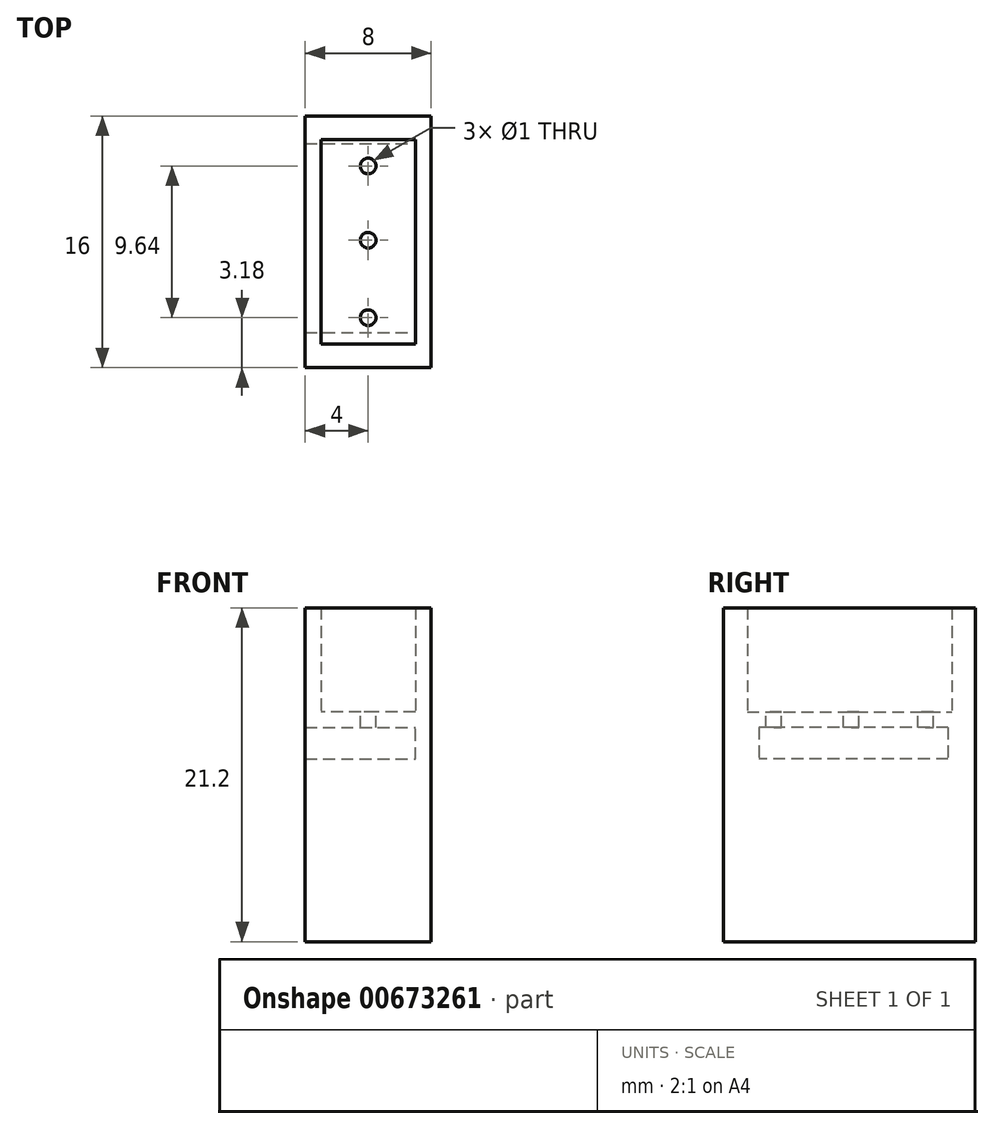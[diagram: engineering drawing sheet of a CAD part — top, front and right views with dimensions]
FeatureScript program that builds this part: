
annotation { "Feature Type Name" : "Feature", "Feature Type Description" : "" }
export const myFeature = defineFeature(function(context is Context, id is Id, definition is map)
    precondition{}
    {
        {
            var Q0;
            Q0=qCreatedBy(makeId("Top.planeOp"),FACE);
            var sketch = newSketch(context, id + "F0", { "sketchPlane" : qUnion([Q0])});
            skLineSegment(sketch, "E0.bottom", {"start": v(0, 0) * mm, "end": v(-6, 0) * mm});
            skLineSegment(sketch, "E0.top", {"start": v(0, 13) * mm, "end": v(-6, 13) * mm});
            skLineSegment(sketch, "E0.left", {"start": v(0, 0) * mm, "end": v(0, 13) * mm});
            skLineSegment(sketch, "E0.right", {"start": v(-6, 0) * mm, "end": v(-6, 13) * mm});
            skLineSegment(sketch, "E1.bottom", {"start": v(1, -1.5) * mm, "end": v(-7, -1.5) * mm});
            skLineSegment(sketch, "E1.top", {"start": v(1, 14.5) * mm, "end": v(-7, 14.5) * mm});
            skLineSegment(sketch, "E1.left", {"start": v(1, -1.5) * mm, "end": v(1, 14.5) * mm});
            skLineSegment(sketch, "E1.right", {"start": v(-7, -1.5) * mm, "end": v(-7, 14.5) * mm});
            skSolve(sketch);
        }
        {
            var Q0;
            Q0 = qSketchRegion(id + "F0", true);
            extrude(context, id + "F1", {"entities" : qUnion([Q0]), "depth" : 6.6 * mm, "offsetDistance" : 25 * mm});
        }
        {
            var Q0;
            Q0=makeQuery(id+"F1.opExtrude","CAP_FACE",FACE,{"disambiguationData":[OSD([sQuery(id+"F0.wireOp",EDGE,"E0.bottom"),sQuery(id+"F0.wireOp",EDGE,"E0.top"),sQuery(id+"F0.wireOp",EDGE,"E0.left"),sQuery(id+"F0.wireOp",EDGE,"E0.right"),sQuery(id+"F0.wireOp",EDGE,"E1.bottom"),sQuery(id+"F0.wireOp",EDGE,"E1.top"),sQuery(id+"F0.wireOp",EDGE,"E1.left"),sQuery(id+"F0.wireOp",EDGE,"E1.right")])],"isStart":true});
            var sketch = newSketch(context, id + "F2", { "sketchPlane" : qUnion([Q0])});
            skLineSegment(sketch, "E2.bottom", {"start": v(-7, 1.5) * mm, "end": v(1, 1.5) * mm});
            skLineSegment(sketch, "E2.top", {"start": v(-7, -14.5) * mm, "end": v(1, -14.5) * mm});
            skLineSegment(sketch, "E2.left", {"start": v(-7, 1.5) * mm, "end": v(-7, -14.5) * mm});
            skLineSegment(sketch, "E2.right", {"start": v(1, 1.5) * mm, "end": v(1, -14.5) * mm});
            skSolve(sketch);
        }
        {
            var Q0;
            Q0 = qSketchRegion(id + "F2", true);
            extrude(context, id + "F3", {"entities" : qUnion([Q0]), "operationType" : NewBodyOperationType.ADD, "depth" : 14.6 * mm, "offsetDistance" : 25 * mm});
        }
        {
            var Q0;
            Q0=qCreatedBy(makeId("Right.planeOp"),FACE);
            var sketch = newSketch(context, id + "F4", { "sketchPlane" : qUnion([Q0])});
            skLineSegment(sketch, "E3.bottom", {"start": v(0.75, -3) * mm, "end": v(12.75, -3) * mm});
            skLineSegment(sketch, "E3.top", {"start": v(0.75, -1) * mm, "end": v(12.75, -1) * mm});
            skLineSegment(sketch, "E3.left", {"start": v(0.75, -3) * mm, "end": v(0.75, -1) * mm});
            skLineSegment(sketch, "E3.right", {"start": v(12.75, -3) * mm, "end": v(12.75, -1) * mm});
            skSolve(sketch);
        }
        {
            var Q0;
            Q0=makeQuery(id+"F3.opExtrude","CAP_FACE",FACE,{"disambiguationData":[OSD([sQuery(id+"F2.wireOp",EDGE,"E2.bottom"),sQuery(id+"F2.wireOp",EDGE,"E2.top"),sQuery(id+"F2.wireOp",EDGE,"E2.left"),sQuery(id+"F2.wireOp",EDGE,"E2.right")])],"isStart":true});
            var sketch = newSketch(context, id + "F5", { "sketchPlane" : qUnion([Q0])});
            skCircle(sketch, "E4", {"center": v(-3, 11.32) * mm, "radius": 0.5 * mm});
            skPoint(sketch, "E4.centerSnap0", {"position": v(-3, 13) * mm});
            skCircle(sketch, "E5", {"center": v(-3, 6.6) * mm, "radius": 0.5 * mm});
            skCircle(sketch, "E6", {"center": v(-3, 1.68) * mm, "radius": 0.5 * mm});
            skSolve(sketch);
        }
        {
            var Q0;
            Q0 = qSketchRegion(id + "F5", true);
            extrude(context, id + "F6", {"entities" : qUnion([Q0]), "operationType" : NewBodyOperationType.REMOVE, "oppositeDirection" : true, "depth" : 3 * mm, "offsetDistance" : 25 * mm});
        }
        {
            var Q0;
            Q0 = qSketchRegion(id + "F4", true);
            extrude(context, id + "F7", {"entities" : qUnion([Q0]), "operationType" : NewBodyOperationType.REMOVE, "oppositeDirection" : true, "depth" : 12 * mm, "offsetDistance" : 25 * mm});
        }
    });
